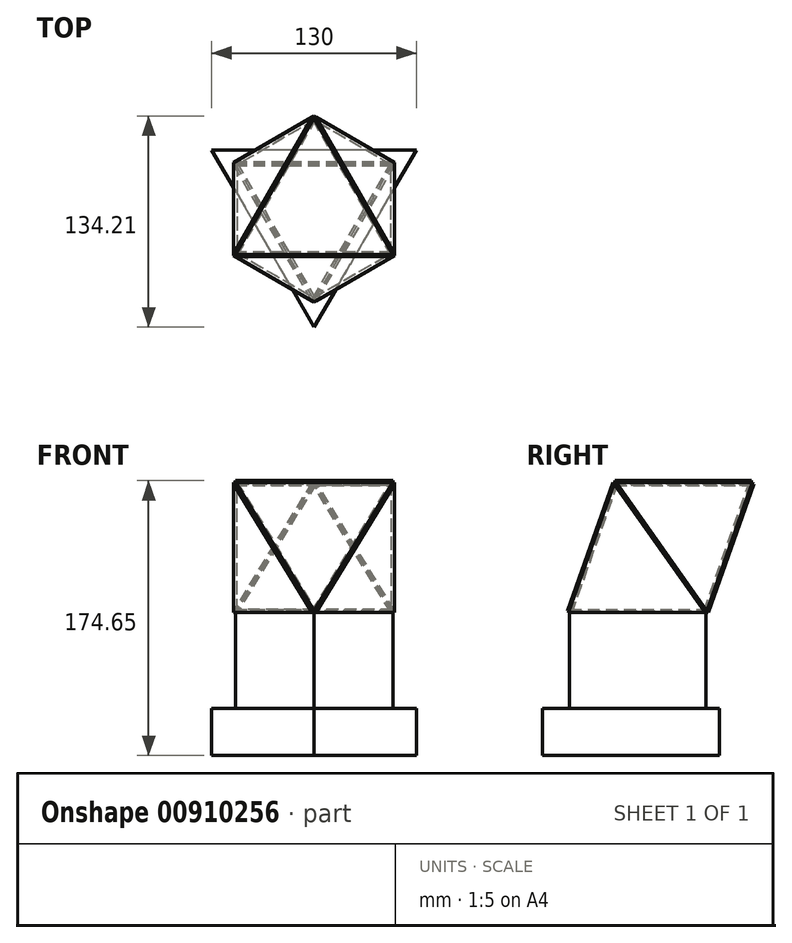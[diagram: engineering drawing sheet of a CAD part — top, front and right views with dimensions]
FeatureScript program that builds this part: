
annotation { "Feature Type Name" : "Feature", "Feature Type Description" : "" }
export const myFeature = defineFeature(function(context is Context, id is Id, definition is map)
    precondition{}
    {
        {
            var Q0;
            Q0=qCreatedBy(makeId("Top.planeOp"),FACE);
            var sketch = newSketch(context, id + "F0", { "sketchPlane" : qUnion([Q0])});
            skCircle(sketch, "E0.cCircle", {"center": v(0, 0) * mm, "radius": 28.87 * mm, "construction": true});
            skLineSegment(sketch, "E0.0", {"start": v(-50, 28.87) * mm, "end": v(50, 28.87) * mm});
            skLineSegment(sketch, "E0.1", {"start": v(50, 28.87) * mm, "end": v(0, -57.74) * mm});
            skLineSegment(sketch, "E0.2", {"start": v(0, -57.74) * mm, "end": v(-50, 28.87) * mm});
            skPoint(sketch, "E0.0.midPoint", {"position": v(0, 28.87) * mm});
            skSolve(sketch);
        }
        {
            var Q0;
            Q0=makeQuery(id+"F0.imprint","IMPRINT",FACE,{"disambiguationData":[TD([[makeQuery(id+"F0.imprint","IMPRINT",EDGE,{"derivedFrom":sQuery(id+"F0.wireOp",EDGE,"E0.0")}),-1.0]])]});
            extrude(context, id + "F1", {"entities" : qUnion([Q0]), "depth" : 3 * mm, "offsetDistance" : 25 * mm});
        }
        {
            var Q0;
            Q0=makeQuery(id+"F1.opExtrude","SWEPT_FACE",FACE,{"disambiguationData":[OSD([sQuery(id+"F0.wireOp",EDGE,"E0.2")])]});
            var sketch = newSketch(context, id + "F2", { "sketchPlane" : qUnion([Q0])});
            skLineSegment(sketch, "E1", {"start": v(-50, 1.5) * mm, "end": v(50, 1.5) * mm});
            skSolve(sketch);
        }
        {
            var Q0;
            Q0=makeQuery(id+"F1.opExtrude","SWEPT_BODY",BODY,{"disambiguationData":[OSD([sQuery(id+"F0.wireOp",EDGE,"E0.0"),sQuery(id+"F0.wireOp",EDGE,"E0.1"),sQuery(id+"F0.wireOp",EDGE,"E0.2")])]});
            transform(context, id + "F3", {"entities" : qUnion([Q0]), "transformType" : TransformType.TRANSLATION_3D, "dx" : 0 * mm, "dy" : 0 * mm, "dz" : 0 * mm, "makeCopy" : true});
        }
        {
            var Q0;
            Q0=makeQuery(id+"F3.opPattern","COPY",BODY,{"derivedFrom":makeQuery(id+"F1.opExtrude","SWEPT_BODY",BODY,{"disambiguationData":[OSD([sQuery(id+"F0.wireOp",EDGE,"E0.0"),sQuery(id+"F0.wireOp",EDGE,"E0.1"),sQuery(id+"F0.wireOp",EDGE,"E0.2")])]}),"instanceName":"1"});
            var Q1;
            Q1=sQuery(id+"F2.wireOp",EDGE,"E1");
            var Q2;
            Q2=sQuery(id+"F2.wireOp",EDGE,"E1");
            transform(context, id + "F4", {"entities" : qUnion([Q0]), "transformType" : TransformType.ROTATION, "transformAxis" : qUnion([Q2]), "angle" : 109.47 * degree, "makeCopy" : false});
        }
        {
            var Q0;
            Q0=makeQuery(id+"F1.opExtrude","SWEPT_BODY",BODY,{"disambiguationData":[OSD([sQuery(id+"F0.wireOp",EDGE,"E0.0"),sQuery(id+"F0.wireOp",EDGE,"E0.1"),sQuery(id+"F0.wireOp",EDGE,"E0.2")])]});
            transform(context, id + "F5", {"entities" : qUnion([Q0]), "transformType" : TransformType.TRANSLATION_3D, "dx" : 0 * mm, "dy" : 0 * mm, "dz" : 0 * mm, "makeCopy" : true});
        }
        {
            var Q0;
            Q0=makeQuery(id+"F1.opExtrude","SWEPT_FACE",FACE,{"disambiguationData":[OSD([sQuery(id+"F0.wireOp",EDGE,"E0.0")])]});
            var sketch = newSketch(context, id + "F6", { "sketchPlane" : qUnion([Q0])});
            skLineSegment(sketch, "E2", {"start": v(50, 1.5) * mm, "end": v(-50, 1.5) * mm});
            skSolve(sketch);
        }
        {
            var Q0;
            Q0=makeQuery(id+"F5.opPattern","COPY",BODY,{"derivedFrom":makeQuery(id+"F1.opExtrude","SWEPT_BODY",BODY,{"disambiguationData":[OSD([sQuery(id+"F0.wireOp",EDGE,"E0.0"),sQuery(id+"F0.wireOp",EDGE,"E0.1"),sQuery(id+"F0.wireOp",EDGE,"E0.2")])]}),"instanceName":"1"});
            var Q1;
            Q1=sQuery(id+"F6.wireOp",EDGE,"E2");
            var Q2;
            Q2=sQuery(id+"F6.wireOp",EDGE,"E2");
            transform(context, id + "F7", {"entities" : qUnion([Q0]), "transformType" : TransformType.ROTATION, "transformAxis" : qUnion([Q2]), "angle" : 109.47 * degree, "oppositeDirection" : true, "makeCopy" : false});
        }
        {
            var Q0;
            Q0=qCreatedBy(makeId("Front.planeOp"),FACE);
            var sketch = newSketch(context, id + "F8", { "sketchPlane" : qUnion([Q0])});
            skLineSegment(sketch, "E3", {"start": v(0, 0) * mm, "end": v(0, 75.98) * mm});
            skSolve(sketch);
        }
        {
            var Q0;
            Q0=makeQuery(id+"F3.opPattern","COPY",BODY,{"derivedFrom":makeQuery(id+"F1.opExtrude","SWEPT_BODY",BODY,{"disambiguationData":[OSD([sQuery(id+"F0.wireOp",EDGE,"E0.0"),sQuery(id+"F0.wireOp",EDGE,"E0.1"),sQuery(id+"F0.wireOp",EDGE,"E0.2")])]}),"instanceName":"1"});
            var Q1;
            Q1=sQuery(id+"F8.wireOp",EDGE,"E3");
            circularPattern(context, id + "F9", {"entities" : qUnion([Q0]), "axis" : qUnion([Q1]), "angle" : 360 * degree, "instanceCount" : 3, "equalSpace" : true});
        }
        {
            var Q0;
            Q0=makeQuery(id+"F5.opPattern","COPY",FACE,{"derivedFrom":makeQuery(id+"F1.opExtrude","SWEPT_FACE",FACE,{"disambiguationData":[OSD([sQuery(id+"F0.wireOp",EDGE,"E0.1")])]}),"instanceName":"1"});
            var sketch = newSketch(context, id + "F10", { "sketchPlane" : qUnion([Q0])});
            skLineSegment(sketch, "E4", {"start": v(21.03, -22.59) * mm, "end": v(50.3, 73.03) * mm});
            skSolve(sketch);
        }
        {
            var Q0;
            Q0=makeQuery(id+"F5.opPattern","COPY",BODY,{"derivedFrom":makeQuery(id+"F1.opExtrude","SWEPT_BODY",BODY,{"disambiguationData":[OSD([sQuery(id+"F0.wireOp",EDGE,"E0.0"),sQuery(id+"F0.wireOp",EDGE,"E0.1"),sQuery(id+"F0.wireOp",EDGE,"E0.2")])]}),"instanceName":"1"});
            var Q1;
            Q1=sQuery(id+"F10.wireOp",EDGE,"E4");
            transform(context, id + "F11", {"entities" : qUnion([Q0]), "transformType" : TransformType.ROTATION, "transformAxis" : qUnion([Q1]), "angle" : 109.47 * degree, "makeCopy" : false});
        }
        {
            var Q0;
            Q0=makeQuery(id+"F5.opPattern","COPY",BODY,{"derivedFrom":makeQuery(id+"F1.opExtrude","SWEPT_BODY",BODY,{"disambiguationData":[OSD([sQuery(id+"F0.wireOp",EDGE,"E0.0"),sQuery(id+"F0.wireOp",EDGE,"E0.1"),sQuery(id+"F0.wireOp",EDGE,"E0.2")])]}),"instanceName":"1"});
            var Q1;
            Q1=sQuery(id+"F8.wireOp",EDGE,"E3");
            circularPattern(context, id + "F12", {"entities" : qUnion([Q0]), "axis" : qUnion([Q1]), "angle" : 360 * degree, "instanceCount" : 3, "equalSpace" : true});
        }
        {
            var Q0;
            Q0=makeQuery(id+"F5.opPattern","COPY",FACE,{"derivedFrom":makeQuery(id+"F1.opExtrude","SWEPT_FACE",FACE,{"disambiguationData":[OSD([sQuery(id+"F0.wireOp",EDGE,"E0.2")])]}),"instanceName":"1"});
            var sketch = newSketch(context, id + "F13", { "sketchPlane" : qUnion([Q0])});
            skLineSegment(sketch, "E5", {"start": v(20.74, 71.33) * mm, "end": v(72.96, -13.95) * mm});
            skSolve(sketch);
        }
        {
            var Q0;
            Q0=makeQuery(id+"F5.opPattern","COPY",BODY,{"derivedFrom":makeQuery(id+"F1.opExtrude","SWEPT_BODY",BODY,{"disambiguationData":[OSD([sQuery(id+"F0.wireOp",EDGE,"E0.0"),sQuery(id+"F0.wireOp",EDGE,"E0.1"),sQuery(id+"F0.wireOp",EDGE,"E0.2")])]}),"instanceName":"1"});
            transform(context, id + "F14", {"entities" : qUnion([Q0]), "transformType" : TransformType.TRANSLATION_3D, "dx" : 0 * mm, "dy" : 0 * mm, "dz" : 0 * mm, "makeCopy" : true});
        }
        {
            var Q0;
            Q0=makeQuery(id+"F14.opPattern","COPY",BODY,{"derivedFrom":makeQuery(id+"F5.opPattern","COPY",BODY,{"derivedFrom":makeQuery(id+"F1.opExtrude","SWEPT_BODY",BODY,{"disambiguationData":[OSD([sQuery(id+"F0.wireOp",EDGE,"E0.0"),sQuery(id+"F0.wireOp",EDGE,"E0.1"),sQuery(id+"F0.wireOp",EDGE,"E0.2")])]}),"instanceName":"1"}),"instanceName":"1"});
            var Q1;
            Q1=sQuery(id+"F13.wireOp",EDGE,"E5");
            var Q2;
            Q2=sQuery(id+"F13.wireOp",EDGE,"E5");
            transform(context, id + "F15", {"entities" : qUnion([Q0]), "transformType" : TransformType.ROTATION, "transformAxis" : qUnion([Q2]), "angle" : 109.47 * degree, "oppositeDirection" : true, "makeCopy" : false});
        }
        {
            var Q0;
            Q0=makeQuery(id+"F1.opExtrude","CAP_FACE",FACE,{"disambiguationData":[OSD([sQuery(id+"F0.wireOp",EDGE,"E0.0"),sQuery(id+"F0.wireOp",EDGE,"E0.1"),sQuery(id+"F0.wireOp",EDGE,"E0.2")])],"isStart":true});
            extrude(context, id + "F16", {"entities" : qUnion([Q0]), "operationType" : NewBodyOperationType.ADD, "depth" : 60 * mm, "offsetDistance" : 25 * mm});
        }
        {
            var Q0;
            Q0=makeQuery(id+"F16.opExtrude","CAP_FACE",FACE,{"disambiguationData":[OSD([sQuery(id+"F0.wireOp",EDGE,"E0.0"),sQuery(id+"F0.wireOp",EDGE,"E0.1"),sQuery(id+"F0.wireOp",EDGE,"E0.2")])],"isStart":false});
            var sketch = newSketch(context, id + "F17", { "sketchPlane" : qUnion([Q0])});
            skCircle(sketch, "E6.cCircle", {"center": v(0, 0) * mm, "radius": 37.53 * mm, "construction": true});
            skLineSegment(sketch, "E6.0", {"start": v(0, 75.06) * mm, "end": v(65, -37.53) * mm});
            skLineSegment(sketch, "E6.1", {"start": v(65, -37.53) * mm, "end": v(-65, -37.53) * mm});
            skLineSegment(sketch, "E6.2", {"start": v(-65, -37.53) * mm, "end": v(0, 75.06) * mm});
            skPoint(sketch, "E6.0.midPoint", {"position": v(32.5, 18.76) * mm});
            skSolve(sketch);
        }
        {
            var Q0;
            Q0 = qSketchRegion(id + "F17", true);
            extrude(context, id + "F18", {"entities" : qUnion([Q0]), "operationType" : NewBodyOperationType.ADD, "depth" : 30 * mm, "offsetDistance" : 25 * mm});
        }
    });
